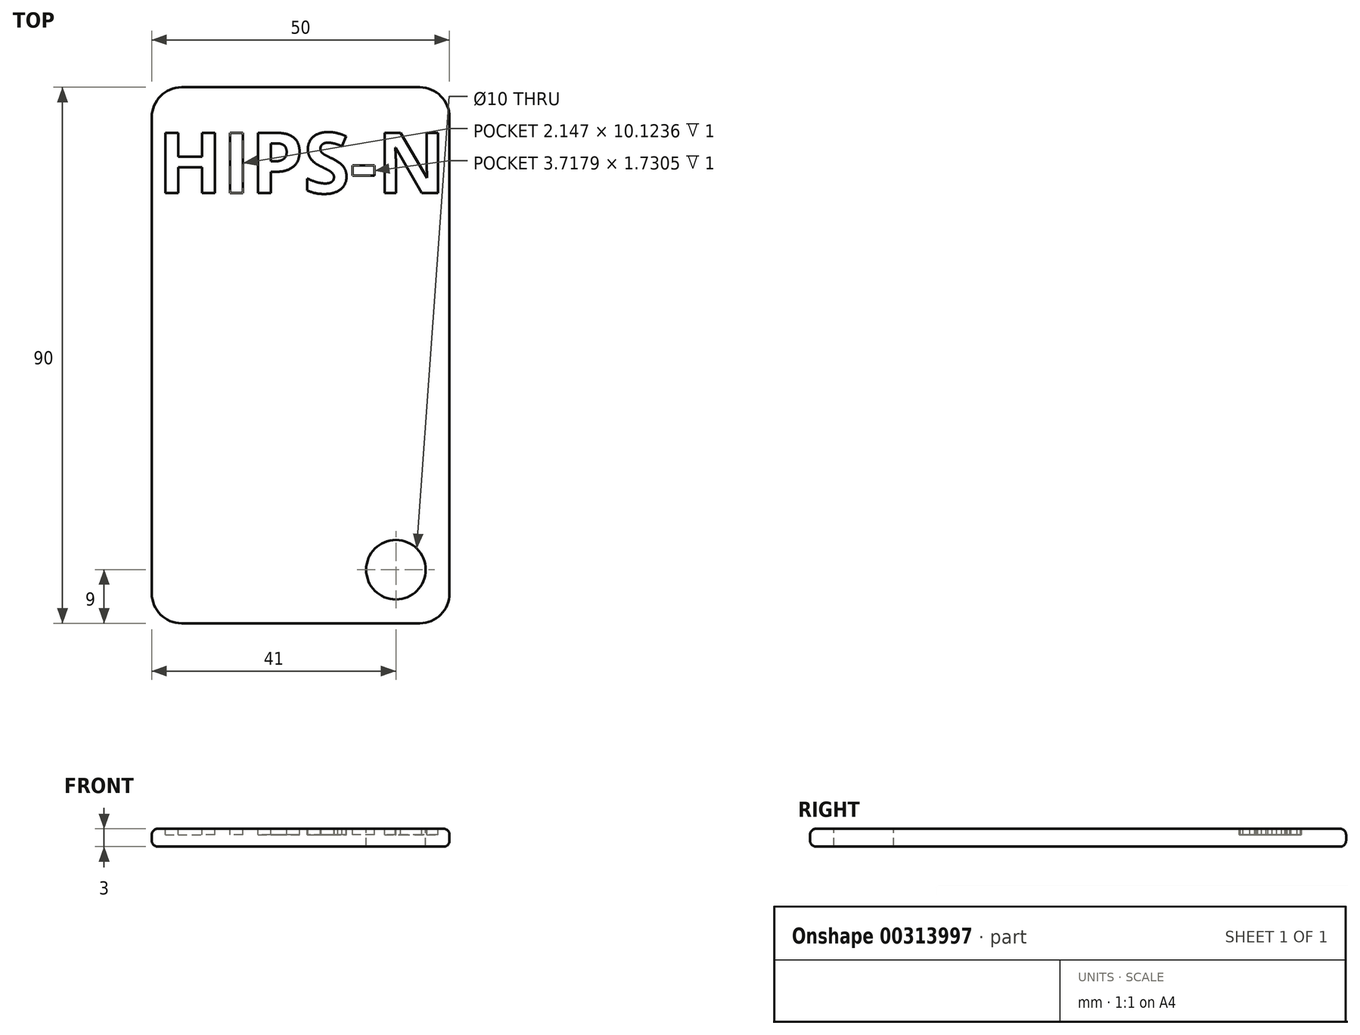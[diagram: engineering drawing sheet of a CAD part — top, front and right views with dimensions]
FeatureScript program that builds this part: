
annotation { "Feature Type Name" : "Feature", "Feature Type Description" : "" }
export const myFeature = defineFeature(function(context is Context, id is Id, definition is map)
    precondition{}
    {
        {
            var Q0;
            Q0=qCreatedBy(makeId("Top.planeOp"),FACE);
            var sketch = newSketch(context, id + "F0", { "sketchPlane" : qUnion([Q0])});
            skLineSegment(sketch, "E0.bottom", {"start": v(-45, 25) * mm, "end": v(45, 25) * mm});
            skLineSegment(sketch, "E0.top", {"start": v(-45, -25) * mm, "end": v(45, -25) * mm});
            skLineSegment(sketch, "E0.left", {"start": v(-45, 25) * mm, "end": v(-45, -25) * mm});
            skLineSegment(sketch, "E0.right", {"start": v(45, 25) * mm, "end": v(45, -25) * mm});
            skLineSegment(sketch, "E1", {"start": v(-45, 25) * mm, "end": v(45, -25) * mm, "construction": true});
            skSolve(sketch);
        }
        {
            var Q0;
            Q0=makeQuery(id+"F0.imprint","IMPRINT",FACE,{"disambiguationData":[TD([[makeQuery(id+"F0.imprint","IMPRINT",EDGE,{"derivedFrom":sQuery(id+"F0.wireOp",EDGE,"E0.bottom")}),-1.0]])]});
            extrude(context, id + "F1", {"entities" : qUnion([Q0]), "depth" : 3 * mm});
        }
        {
            var Q0;
            Q0=makeQuery(id+"F1.opExtrude","CAP_FACE",FACE,{"disambiguationData":[OSD([sQuery(id+"F0.wireOp",EDGE,"E0.bottom"),sQuery(id+"F0.wireOp",EDGE,"E0.top"),sQuery(id+"F0.wireOp",EDGE,"E0.left"),sQuery(id+"F0.wireOp",EDGE,"E0.right")])],"isStart":false});
            var Q1;
            Q1=makeQuery(id+"F1.opExtrude","CAP_FACE",FACE,{"disambiguationData":[OSD([sQuery(id+"F0.wireOp",EDGE,"E0.bottom"),sQuery(id+"F0.wireOp",EDGE,"E0.top"),sQuery(id+"F0.wireOp",EDGE,"E0.left"),sQuery(id+"F0.wireOp",EDGE,"E0.right")])],"isStart":true});
            fillet(context, id + "F2", {"entities" : qUnion([Q0, Q1]), "radius" : 1 * mm, "tangentPropagation" : true, "allowEdgeOverflow" : false});
        }
        {
            var Q0;
            Q0=makeQuery(id+"F1.opExtrude","SWEPT_EDGE",EDGE,{"disambiguationData":[OSD([sQuery(id+"F0.wireOp",EDGE,"E0.top"),sQuery(id+"F0.wireOp",EDGE,"E0.right")])]});
            var Q1;
            Q1=makeQuery(id+"F1.opExtrude","SWEPT_EDGE",EDGE,{"disambiguationData":[OSD([sQuery(id+"F0.wireOp",EDGE,"E0.bottom"),sQuery(id+"F0.wireOp",EDGE,"E0.right")])]});
            var Q2;
            Q2=makeQuery(id+"F1.opExtrude","SWEPT_EDGE",EDGE,{"disambiguationData":[OSD([sQuery(id+"F0.wireOp",EDGE,"E0.bottom"),sQuery(id+"F0.wireOp",EDGE,"E0.left")])]});
            var Q3;
            Q3=makeQuery(id+"F1.opExtrude","SWEPT_EDGE",EDGE,{"disambiguationData":[OSD([sQuery(id+"F0.wireOp",EDGE,"E0.top"),sQuery(id+"F0.wireOp",EDGE,"E0.left")])]});
            fillet(context, id + "F3", {"entities" : qUnion([Q0, Q1, Q2, Q3]), "radius" : 5 * mm, "tangentPropagation" : true, "allowEdgeOverflow" : false});
        }
        {
            var Q0;
            Q0=qCreatedBy(makeId("Right.planeOp"),FACE);
            var sketch = newSketch(context, id + "F4", { "sketchPlane" : qUnion([Q0])});
            skLineSegment(sketch, "E2", {"start": v(0, 0) * mm, "end": v(0, 32.9) * mm});
            skSolve(sketch);
        }
        {
            var Q0;
            Q0=makeQuery(id+"F1.opExtrude","SWEPT_BODY",BODY,{"disambiguationData":[OSD([sQuery(id+"F0.wireOp",EDGE,"E0.bottom"),sQuery(id+"F0.wireOp",EDGE,"E0.top"),sQuery(id+"F0.wireOp",EDGE,"E0.left"),sQuery(id+"F0.wireOp",EDGE,"E0.right")])]});
            var Q1;
            Q1=sQuery(id+"F4.wireOp",EDGE,"E2");
            transform(context, id + "F5", {"entities" : qUnion([Q0]), "transformType" : TransformType.ROTATION, "transformAxis" : qUnion([Q1]), "angle" : 90 * degree, "makeCopy" : false});
        }
        {
            var Q0;
            Q0=makeQuery(id+"F1.opExtrude","CAP_FACE",FACE,{"disambiguationData":[OSD([sQuery(id+"F0.wireOp",EDGE,"E0.bottom"),sQuery(id+"F0.wireOp",EDGE,"E0.top"),sQuery(id+"F0.wireOp",EDGE,"E0.left"),sQuery(id+"F0.wireOp",EDGE,"E0.right")])],"isStart":false});
            var sketch = newSketch(context, id + "F6", { "sketchPlane" : qUnion([Q0])});
            skText(sketch, "E3", { "text": "HIPS-N", "fontName": "OpenSans-Bold.ttf"});
            const initialGuessF6  = {"E3": [-0.024, 0.02722, 1, 0, 0.01021]};
            skSetInitialGuess(sketch, initialGuessF6);
            skSolve(sketch);
        }
        {
            var Q0;
            Q0=qSketchRegion(id+"F6",true);
            extrude(context, id + "F7", {"entities" : qUnion([Q0]), "operationType" : NewBodyOperationType.REMOVE, "oppositeDirection" : true, "depth" : 1 * mm});
        }
        {
            var Q0;
            {var subQ0=sQuery(id+"F0.wireOp",EDGE,"E0.left");var subQ2=sQuery(id+"F0.wireOp",EDGE,"E0.bottom");var subQ4=sQuery(id+"F0.wireOp",EDGE,"E0.right");var subQ6=sQuery(id+"F0.wireOp",EDGE,"E0.top");Q0=makeQuery(id+"F7.boolean.opBoolean","SPLIT",FACE,{"disambiguationData":[TD([makeQuery(id+"F7.opExtrude","SWEPT_FACE",FACE,{"disambiguationData":[OSD([sQuery(id+"F6.wireOp",EDGE,"E3.sketch_text.stroke-0")])]})])],"derivedFrom":makeQuery(id+"F1.opExtrude","CAP_FACE",FACE,{"disambiguationData":[OSD([subQ2,subQ6,subQ0,subQ4])],"isStart":false})});}
            var sketch = newSketch(context, id + "F8", { "sketchPlane" : qUnion([Q0])});
            skCircle(sketch, "E4", {"center": v(16, -36) * mm, "radius": 5 * mm});
            skSolve(sketch);
        }
        {
            var Q0;
            Q0=qSketchRegion(id+"F8",true);
            extrude(context, id + "F9", {"entities" : qUnion([Q0]), "operationType" : NewBodyOperationType.REMOVE, "oppositeDirection" : true, "depth" : 3 * mm});
        }
    });
